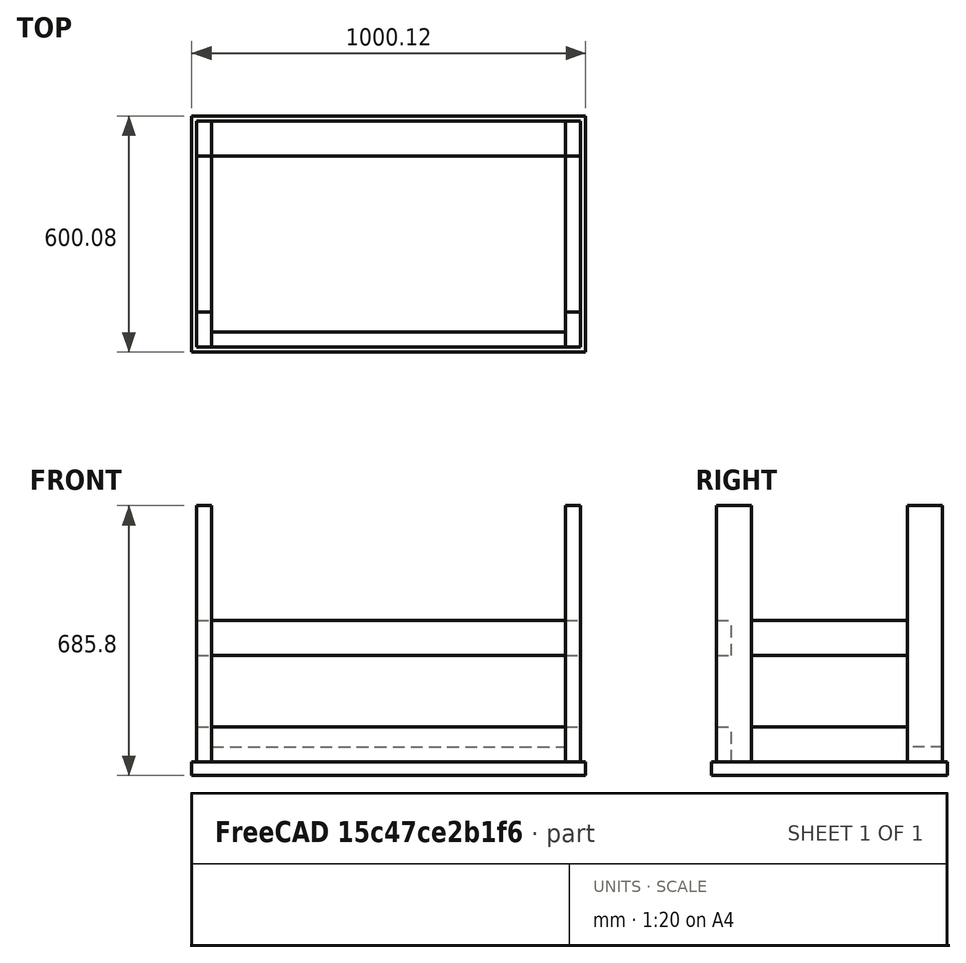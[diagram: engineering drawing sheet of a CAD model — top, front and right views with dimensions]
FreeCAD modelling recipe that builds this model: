
FCSTD DOCUMENT  (FreeCAD 0.18R16146 (Git))
Label: desk_small_top
License: All rights reserved
LicenseURL: http://en.wikipedia.org/wiki/All_rights_reserved
objects: Part::Box×12, TechDraw::DrawViewDimension×8, TechDraw::DrawViewPart×4, TechDraw::DrawSVGTemplate×1, Part::Compound×1, TechDraw::DrawPage×1
note: 13 computed .brp shape members not serialized (recipe doc carries the construction recipe); baked Part::Feature solids carry a one-line shape summary decoded from their .brp

FEATURE [Part::Box] Box  label="tabletop"
  AttacherType = Attacher::AttachEngine3D
  Height = 34.925
  Length = 1000.12
  Width = 600.075
FEATURE [Part::Box] Box001  label="Leg back right"
  AttacherType = Attacher::AttachEngine3D
  Height = 650.875
  Length = 38.1
  Placement = pos=(12.7,12.7,34.925) rot=(0,0,1;0rad)
  Width = 88.9
FEATURE [Part::Box] Box002  label="Leg front right"
  AttacherType = Attacher::AttachEngine3D
  Height = 650.875
  Length = 38.1
  Placement = pos=(12.7,498.475,34.925) rot=(0,0,1;0rad)
  Width = 88.9
FEATURE [Part::Box] Box003  label="Leg front left"
  AttacherType = Attacher::AttachEngine3D
  Height = 650.875
  Length = 38.1
  Placement = pos=(949.325,498.475,34.925) rot=(0,0,1;0rad)
  Width = 88.9
FEATURE [Part::Box] Box004  label="Leg back left"
  AttacherType = Attacher::AttachEngine3D
  Height = 650.875
  Length = 38.1
  Placement = pos=(949.325,12.7,34.925) rot=(0,0,1;0rad)
  Width = 88.9
FEATURE [Part::Box] Box005  label="back lower brace"
  AttacherType = Attacher::AttachEngine3D
  Height = 88.9
  Length = 898.525
  Placement = pos=(50.8,12.7,304.8) rot=(0,0,1;0rad)
  Width = 38.1
FEATURE [Part::Box] Box006  label="back upper brace"
  AttacherType = Attacher::AttachEngine3D
  Height = 88.9
  Length = 898.525
  Placement = pos=(50.8,12.7,34.925) rot=(0,0,1;0rad)
  Width = 38.1
FEATURE [Part::Box] Box007  label="side right lower brace"
  AttacherType = Attacher::AttachEngine3D
  Height = 88.9
  Length = 38.1
  Placement = pos=(12.7,101.6,304.8) rot=(0,0,1;0rad)
  Width = 396.875
FEATURE [Part::Box] Box008  label="side right upper brace"
  AttacherType = Attacher::AttachEngine3D
  Height = 88.9
  Length = 38.1
  Placement = pos=(12.7,101.6,34.925) rot=(0,0,1;0rad)
  Width = 396.875
FEATURE [Part::Box] Box009  label="side left upper brace"
  AttacherType = Attacher::AttachEngine3D
  Height = 88.9
  Length = 38.1
  Placement = pos=(949.325,101.6,34.925) rot=(0,0,1;0rad)
  Width = 396.875
FEATURE [Part::Box] Box010  label="side left lower brace"
  AttacherType = Attacher::AttachEngine3D
  Height = 88.9
  Length = 38.1
  Placement = pos=(949.325,101.6,304.8) rot=(0,0,1;0rad)
  Width = 396.875
FEATURE [TechDraw::DrawSVGTemplate] Template
  EditableTexts = Designed_by_Name=Sean Fischer; Drawing_number=1/1; FC-Date=1/16/20; FC-SC=1; FC-SH=1/1; FC-Title=Desk (Small Top)
  Height = 210
  Orientation = 1
  Width = 297
FEATURE [Part::Box] Box011  label="front upper brace"
  AttacherType = Attacher::AttachEngine3D
  Height = 88.9
  Length = 898.525
  Placement = pos=(50.8,587.375,34.925) rot=(1,0,0;1.5708rad)
  Width = 38.1
FEATURE [Part::Compound] Compound  label="Desk Frame"
  Links = -> [Box001,Box002,Box003,Box004,Box005,Box006,Box007,Box008,Box009,Box010,Box011]
FEATURE [TechDraw::DrawViewPart] View  label="Iso"
  CoarseView = false
  Direction = (-0.577,0.577,0.577)
  Focus = 100
  HardHidden = false
  IsoCount = 0
  IsoHidden = false
  IsoVisible = false
  LockPosition = false
  Perspective = false
  Rotation = 0
  Scale = 0.08
  ScaleType = 2
  SeamHidden = false
  SeamVisible = false
  SmoothHidden = false
  SmoothVisible = false
  Source = -> [Compound]
  X = 80
  Y = 140
FEATURE [TechDraw::DrawViewPart] View001  label="rear"
  CoarseView = false
  Direction = (0,-1,0)
  Focus = 100
  HardHidden = false
  IsoCount = 0
  IsoHidden = false
  IsoVisible = false
  LockPosition = false
  Perspective = false
  Rotation = 0
  Scale = 0.08
  ScaleType = 0
  SeamHidden = false
  SeamVisible = false
  SmoothHidden = false
  SmoothVisible = false
  Source = -> [Compound]
  X = 180
  Y = 140
FEATURE [TechDraw::DrawViewPart] View002  label="front"
  CoarseView = false
  Direction = (0,1,0)
  Focus = 100
  HardHidden = false
  IsoCount = 0
  IsoHidden = false
  IsoVisible = false
  LockPosition = false
  Perspective = false
  Rotation = 0
  Scale = 0.08
  ScaleType = 0
  SeamHidden = false
  SeamVisible = false
  SmoothHidden = false
  SmoothVisible = false
  Source = -> [Compound]
  X = 80
  Y = 50
FEATURE [TechDraw::DrawViewPart] View003  label="side"
  CoarseView = false
  Direction = (-1,0,0)
  Focus = 100
  HardHidden = false
  IsoCount = 0
  IsoHidden = false
  IsoVisible = false
  LockPosition = false
  Perspective = false
  Rotation = 0
  Scale = 0.08
  ScaleType = 0
  SeamHidden = false
  SeamVisible = false
  SmoothHidden = false
  SmoothVisible = false
  Source = -> [Compound]
  X = 255
  Y = 140.509
  expr: X = 255
FEATURE [TechDraw::DrawViewDimension] Dimension
  Arbitrary = false
  FormatSpec = %.2f
  LockPosition = false
  MeasureType = 1
  OverTolerance = 0
  References2D = -> [View001]
  Rotation = 0
  ScaleType = 0
  Type = 1
  UnderTolerance = 0
  X = 0.254357
  Y = 42.3139
FEATURE [TechDraw::DrawViewDimension] Dimension001
  Arbitrary = false
  FormatSpec = %.2f
  LockPosition = false
  MeasureType = 1
  OverTolerance = 0
  References2D = -> [View001]
  Rotation = 0
  ScaleType = 0
  Type = 1
  UnderTolerance = 0
  X = -21.6948
  Y = -37.9898
FEATURE [TechDraw::DrawViewDimension] Dimension004
  Arbitrary = false
  FormatSpec = %.2f
  LockPosition = false
  MeasureType = 1
  OverTolerance = 0
  References2D = -> [View003]
  Rotation = 0
  ScaleType = 0
  Type = 1
  UnderTolerance = 0
  X = 2.03486
  Y = 41.2964
FEATURE [TechDraw::DrawViewDimension] Dimension011
  Arbitrary = false
  FormatSpec = %.2f
  LockPosition = false
  MeasureType = 1
  OverTolerance = 0
  References2D = -> [View002]
  Rotation = 0
  ScaleType = 0
  Type = 2
  UnderTolerance = 0
  X = 45.6023
  Y = -0.254357
FEATURE [TechDraw::DrawViewDimension] Dimension012
  Arbitrary = false
  FormatSpec = %.2f
  LockPosition = false
  MeasureType = 1
  OverTolerance = 0
  References2D = -> [View001]
  Rotation = 0
  ScaleType = 0
  Type = 2
  UnderTolerance = 0
  X = -25.0036
  Y = 14.351
FEATURE [TechDraw::DrawViewDimension] Dimension013
  Arbitrary = false
  FormatSpec = %.2f
  LockPosition = false
  MeasureType = 1
  OverTolerance = 0
  References2D = -> [View001]
  Rotation = 0
  ScaleType = 0
  Type = 2
  UnderTolerance = 0
  X = -24.4949
  Y = -11.684
FEATURE [TechDraw::DrawViewDimension] Dimension014
  Arbitrary = false
  FormatSpec = %.2f
  LockPosition = false
  MeasureType = 1
  OverTolerance = 0
  References2D = -> [View003]
  Rotation = 0
  ScaleType = 0
  Type = 0
  UnderTolerance = 0
  X = -1.27179
  Y = -54.0143
FEATURE [TechDraw::DrawViewDimension] Dimension015
  Arbitrary = false
  FormatSpec = %.2f
  LockPosition = false
  MeasureType = 1
  OverTolerance = 0
  References2D = -> [View003]
  Rotation = 0
  ScaleType = 0
  Type = 1
  UnderTolerance = 0
  X = -1.01743
  Y = -36.9724
FEATURE [TechDraw::DrawPage] Page
  KeepUpdated = true
  ProjectionType = 0
  Template = -> Template
  Views = -> [View,View001,View002,View003,Dimension,Dimension001,Dimension004,Dimension011,Dimension012,Dimension013,Dimension014,Dimension015]
